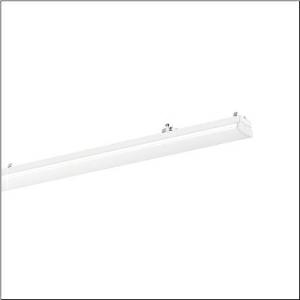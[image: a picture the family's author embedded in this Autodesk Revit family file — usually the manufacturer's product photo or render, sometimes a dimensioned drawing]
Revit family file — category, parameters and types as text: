
# Revit family: licross_r__11_recessed_opal_mo_51tl1ddn425g_3105
name_source: partatom
category: Lighting Fixtures
units: mm (PartAtom-declared; Revit-internal decimal feet)

## family parameters
Cut with Voids When Loaded = No
Host = Face
Light Source = No
Part Type = Normal
Room Calculation Point = No
Round Connector Dimension = Use Diameter
Shared = No

## types (1)
- --- (1 x LED, 2750 lm, 15.7 W, 4000K)
    Apparent Load = 16 VA
    CIE Flux Codes = 44 73 91 87 100
    Color Rendering = 80
    Color Temperature = 4000K
    Default Elevation = 1800 mm
    Description = Licross® 11 recessed opal MO, luminaire insert, of sheet steel, coil coated, white, length: 1.500mm, width: 76mm, height: 87mm, LED rated luminous flux: 2.750lm, light colour: 840, control gear: DALI 2, with plug, 5-pole, with phase selection, mains connection: 220..240V, AC, 50/60Hz, rated input power: 16W, internal wiring halogen-free, primary optical cover: cover, of PMMA, light emission: direct with ceiling illumination distribution, primary light characteristic: symmetric, protection rating (complete): IP40, insulation class (complete): insulation class I (protective earthing), certification: CE, ENEC, VDE, UKCA, protection symbol: D if used in an environment without relevant dust loads with corresponding accessories, impact resistance: IK06, permissible ambient temperature for indoor applications: -25..+50°C, corresponds to IFS (International Featured Standards) requirements for safety and quality in the food industry, reducing of maximum allowable ambient temperature of 5°C with ceiling mounting, LABS conformity tested according to VDMA 24364:2018-05, packaging unit: 1 piece
    Height = 83 mm
    Lamp = 1 x LED
    Lamp Light Flux = 2750 lm
    Lamp Power = 15.7 W
    Lamp count = 1
    Length = 1500 mm
    Luminous efficacy = 175 lm/W
    Manufacturer = Siteco
    ModVariant = No
    Model = 51TL1DDN425G
    Mounting Place = Ceiling
    Mounting Type = Pendant
    Number of Poles = 1
    OnlyDefault = Yes
    Power Factor = 1
    Product Name = Licross® 11 recessed opal MO
    Product group = luminaire insert | ceiling pendant
    ProductGroupID = 902
    Protection Class = Protection class I
    Protection Degree = IP 40
    RLX_Detail_Level = 1
    RLX_Emergency_Light_Flux = 0 lm
    RLX_Emergency_Type = 0
    RLX_Emergency_Type_DB = No
    RlxData = <blob elided: 26429 chars, md5=9f6f0d6a>
    Socket = socket
    Standby Power = 0 W
    System Light Flux = 2750 lm
    System Power = 16 W
    Type Comments = factory setting: luminous flux: 100 % | dim-lin: 254 | 101 mA
    Type Image = l_1313666.jpg
    URL = http://relux.com
    VarID = @adj_097791
    Voltage = 0 V
    Weight = 0.00 kg
    Width = 76 mm

## geometry (parser evidence)
native form markers: Blend x4, Sweep x11
no freeform markers — native parametric forms only
